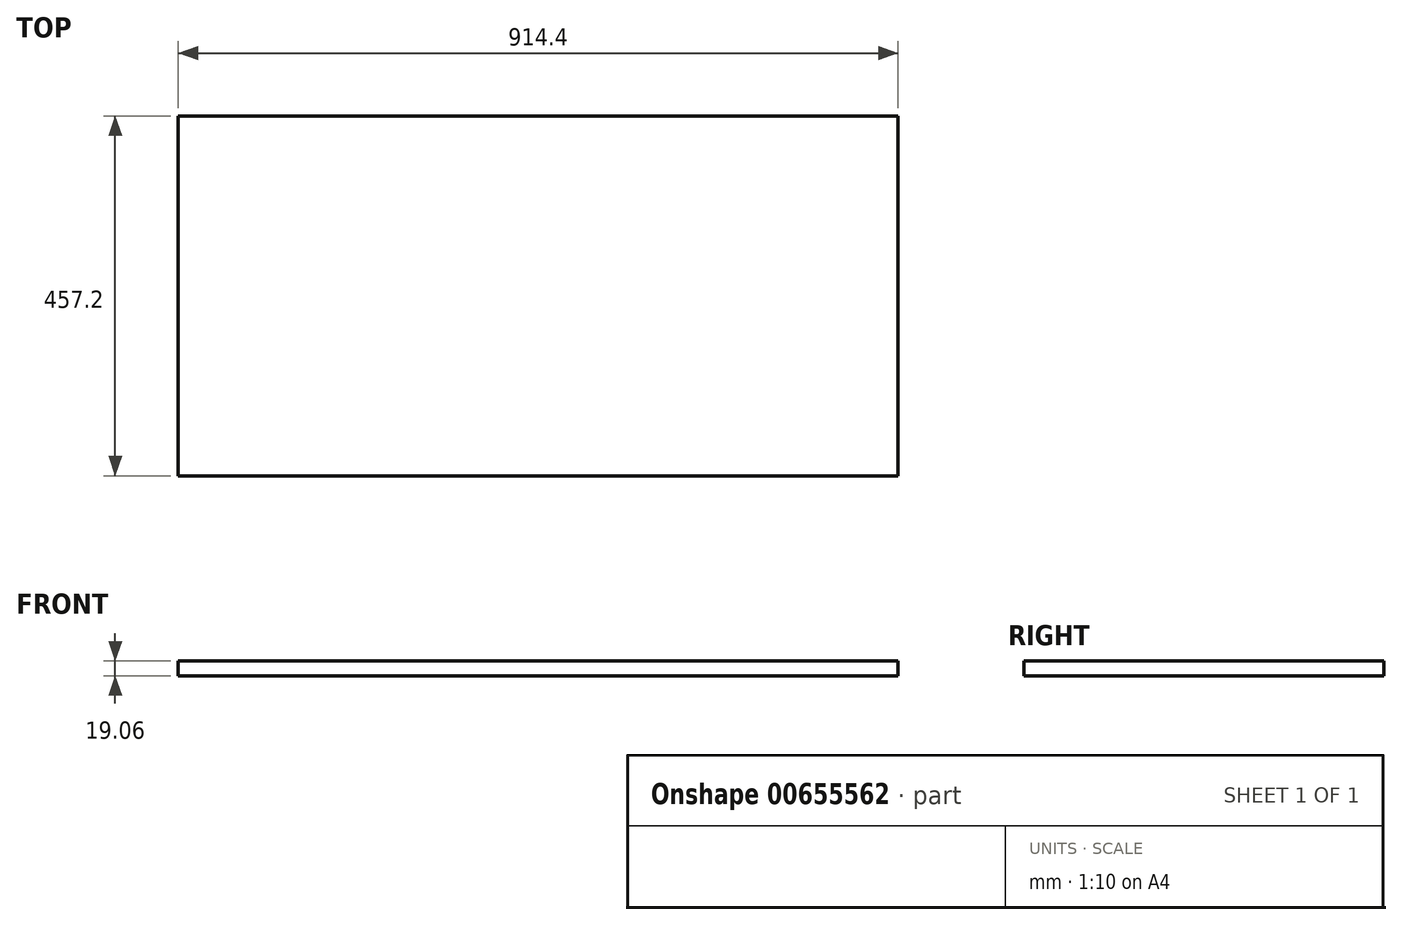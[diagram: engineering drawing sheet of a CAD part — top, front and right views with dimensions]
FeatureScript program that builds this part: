
annotation { "Feature Type Name" : "Feature", "Feature Type Description" : "" }
export const myFeature = defineFeature(function(context is Context, id is Id, definition is map)
    precondition{}
    {
        {
            var Q0;
            Q0=qCreatedBy(makeId("Top.planeOp"),FACE);
            var sketch = newSketch(context, id + "F0", { "sketchPlane" : qUnion([Q0])});
            skLineSegment(sketch, "E0.bottom", {"start": v(-457.2, 228.6) * mm, "end": v(457.2, 228.6) * mm});
            skLineSegment(sketch, "E0.top", {"start": v(-457.2, -228.6) * mm, "end": v(457.2, -228.6) * mm});
            skLineSegment(sketch, "E0.left", {"start": v(-457.2, 228.6) * mm, "end": v(-457.2, -228.6) * mm});
            skLineSegment(sketch, "E0.right", {"start": v(457.2, 228.6) * mm, "end": v(457.2, -228.6) * mm});
            skPoint(sketch, "E0.middle", {"position": v(0, 0) * mm});
            skSolve(sketch);
        }
        {
            var Q0;
            Q0=makeQuery(id+"F0.imprint","IMPRINT",FACE,{"disambiguationData":[TD([[makeQuery(id+"F0.imprint","IMPRINT",EDGE,{"derivedFrom":sQuery(id+"F0.wireOp",EDGE,"E0.bottom")}),-1.0]])]});
            extrude(context, id + "F1", {"entities" : qUnion([Q0]), "endBound" : BoundingType.SYMMETRIC, "depth" : 19.05 * mm, "offsetDistance" : 25.4 * mm});
        }
    });
